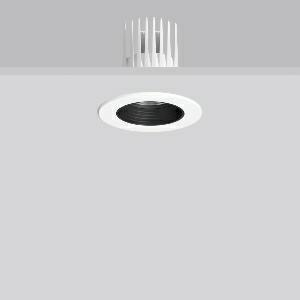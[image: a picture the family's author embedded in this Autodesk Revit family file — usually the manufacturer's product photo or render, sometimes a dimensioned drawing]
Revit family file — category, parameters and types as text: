
# Revit family: heledon_mini_e_901754_002_3_76_c24d
name_source: partatom
category: Lighting Fixtures
units: mm (PartAtom-declared; Revit-internal decimal feet)

## family parameters
Cut with Voids When Loaded = No
Host = Face
Light Source = No
Part Type = Normal
Room Calculation Point = No
Round Connector Dimension = Use Diameter
Shared = No

## types (1)
- HELEDON mini E (1 x LED Modul 935, 3300 lm, 3500)
    Apparent Load = 29 VA
    Approval mark = CE
    CIE Flux Codes = 80 99 100 100 100
    Color Rendering = 92
    Color Temperature = 3500
    Default Elevation = 1800 mm
    Description = Series: HELEDON mini
Round recessed downlight. Housing: die-cast aluminium, powder-coated. Black plastic ring and recessed LED to prevent glare from the side. Optical assembly with lens made of plastic (polycarbonate) for the best homogeneous light distribution - can be changed without tools. Best colour rendering index Ra>90. Suitable for Recessed ceiling mounting. Installation without tools thanks to spring fastening system. Including separate LED converter with connecting cable 600 mm.High quality converter without flickering and stroboscopic effect. Through-wiring box (5 pole) available as accessory. The following accessories can be mounted without use of tools: interchangeable lenses, decorative glasses, honeycomb louvre, clear and frosted diffusers, white interchangeable plastic ring. 
Colour: traffic white, matt (RAL 9016)
Diameter: 124 mm
Height: 3 mm
Cut-out diameter: 114 mm
Recess height: 170 mm
Luminaire: recess height: 120 mm
Lamp: LED
Socket: without socket
Colour temperature: 3500K
Colour rendering index (CRI): 92
System power: 29 W
Rated luminous flux: 3300 lm
Luminous efficiency: 114 lm/W
Control gear: Converter, dimmable, DALI
Protection class: II
Type of protection: IP 20
    Height = 0 mm  [stored 0 ft]
    Lamp = 1 x LED Modul 935
    Lamp Light Flux = 3300 lm
    Lamp count = 1
    Length = 124 mm  [stored 0.406824 ft]
    Lifetime = 50000 h
    Luminous efficacy = 114 lm/W
    Manufacturer = RZB
    ModVariant = No
    Model = 901754.002.3.76
    Mounting Place = Ceiling
    Mounting Type = Recessed
    Number of Poles = 1
    OnlyDefault = Yes
    Power Factor = 1
    Product Name = HELEDON mini E
    Product group = Recessed downlights
    ProductGroupID = 402
    Protection Class = Protection class II
    Protection Degree = IP 20
    RLX_Detail_Level = 1
    RLX_Emergency_Light_Flux = 0 lm
    RLX_Emergency_Type = 0
    RLX_Emergency_Type_DB = No
    RlxData = <blob elided: 125829 chars, md5=a06a1409>
    Socket = socket
    Standby Power = 0 W
    System Light Flux = 3300 lm
    System Power = 29 W
    Type Comments = Product without accessories
    Type Image = 901656.002.jpg
    URL = http://relux.com
    VarID = ---
    Voltage = 230 V
    Voltage Range = 220-240 V
    Weight = 0.00 kg
    Width = 0 mm  [stored 0 ft]

note: [stored X ft] marks values corroborated as IEEE doubles in the binary element streams (Revit-internal decimal feet)

## geometry (parser evidence)
native form markers: Blend x4, Sweep x11
no freeform markers — native parametric forms only
